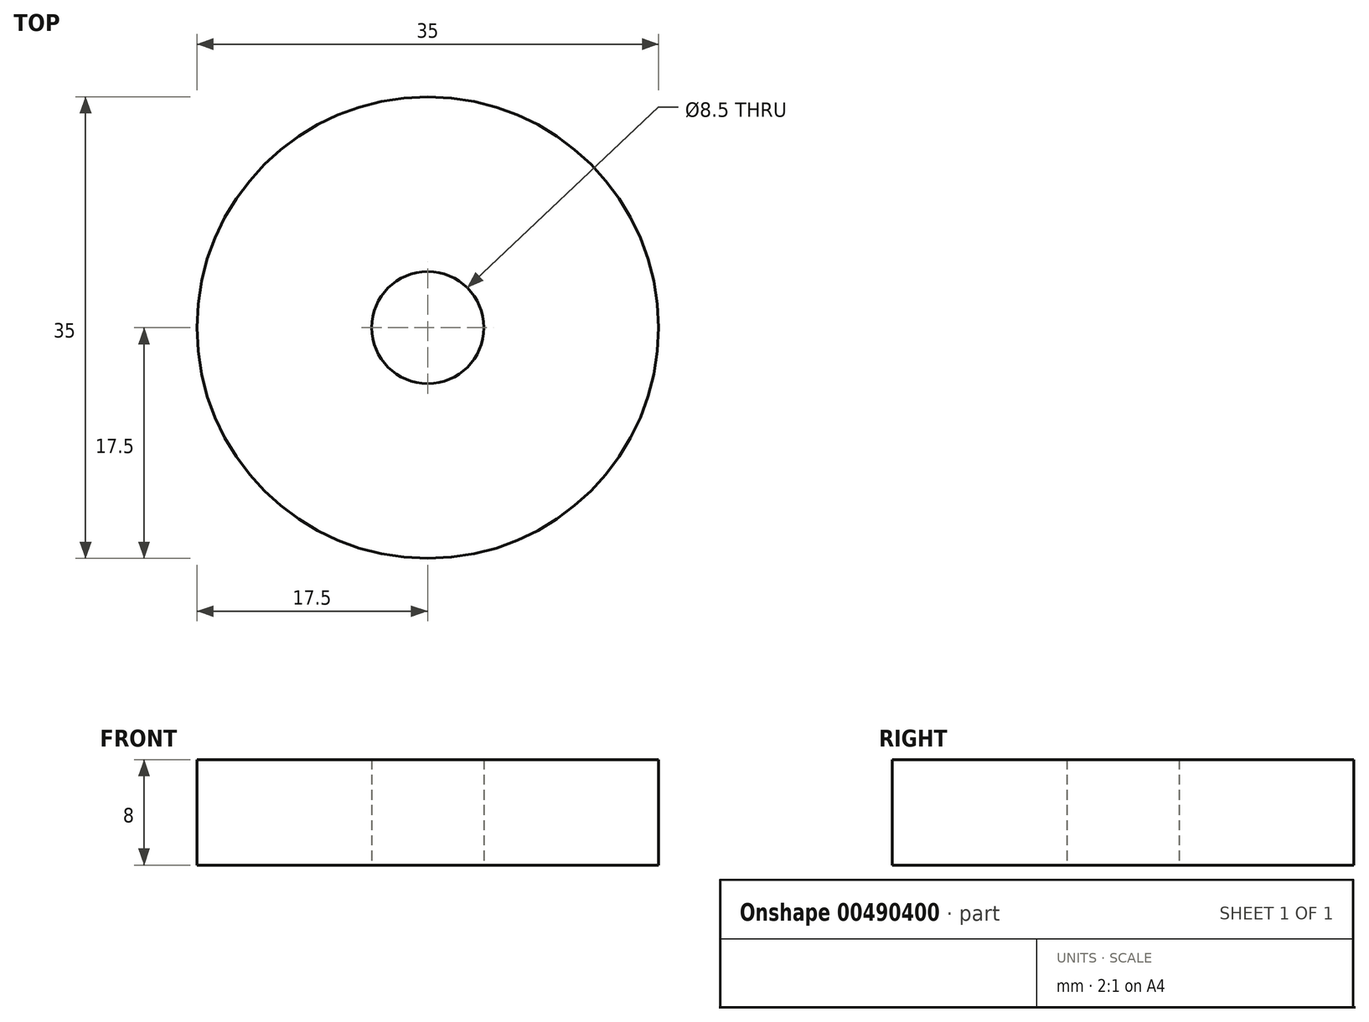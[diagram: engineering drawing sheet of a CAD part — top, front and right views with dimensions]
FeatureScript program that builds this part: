
annotation { "Feature Type Name" : "Feature", "Feature Type Description" : "" }
export const myFeature = defineFeature(function(context is Context, id is Id, definition is map)
    precondition{}
    {
        {
            var Q0;
            Q0=qCreatedBy(makeId("Top.planeOp"),FACE);
            var sketch = newSketch(context, id + "F0", { "sketchPlane" : qUnion([Q0])});
            skCircle(sketch, "E0", {"center": v(0, 0) * mm, "radius": 4.25 * mm});
            skCircle(sketch, "E1", {"center": v(0, 0) * mm, "radius": 17.5 * mm});
            skCircle(sketch, "E2", {"center": v(0, 0) * mm, "radius": 35 * mm});
            skSolve(sketch);
        }
        {
            var Q0;
            Q0=makeQuery(id+"F0.imprint","IMPRINT",FACE,{"disambiguationData":[TD([[makeQuery(id+"F0.imprint","IMPRINT",EDGE,{"derivedFrom":sQuery(id+"F0.wireOp",EDGE,"E0")}),-1.0]])]});
            extrude(context, id + "F1", {"entities" : qUnion([Q0]), "depth" : 8 * mm, "offsetDistance" : 25 * mm});
        }
    });
